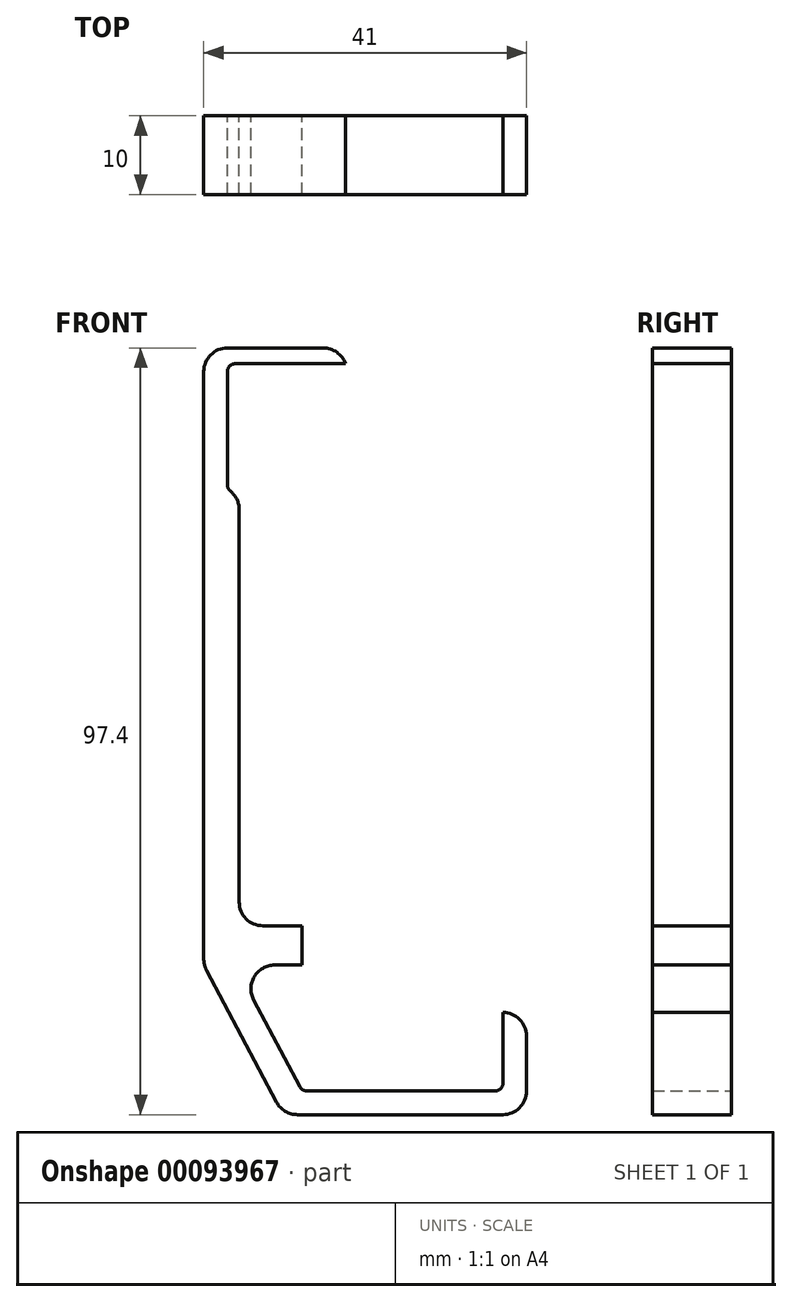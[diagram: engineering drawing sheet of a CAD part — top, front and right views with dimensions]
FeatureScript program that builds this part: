
annotation { "Feature Type Name" : "Feature", "Feature Type Description" : "" }
export const myFeature = defineFeature(function(context is Context, id is Id, definition is map)
    precondition{}
    {
        {
            var Q0;
            Q0=qCreatedBy(makeId("Front.planeOp"),FACE);
            var sketch = newSketch(context, id + "F0", { "sketchPlane" : qUnion([Q0])});
            skLineSegment(sketch, "E0.bottom", {"start": v(50, 8.2) * mm, "end": v(-50, 8.2) * mm});
            skLineSegment(sketch, "E0.top", {"start": v(50, -8.2) * mm, "end": v(-50, -8.2) * mm});
            skLineSegment(sketch, "E0.left", {"start": v(50, 8.2) * mm, "end": v(50, -8.2) * mm});
            skLineSegment(sketch, "E0.right", {"start": v(-50, 8.2) * mm, "end": v(-50, -8.2) * mm});
            skPoint(sketch, "E0.middle", {"position": v(0, 0) * mm});
            skLineSegment(sketch, "E1", {"start": v(-50, -8.2) * mm, "end": v(-40.5, -8.2) * mm});
            skLineSegment(sketch, "E2.bottom", {"start": v(-40.5, -8.2) * mm, "end": v(-15, -8.2) * mm});
            skLineSegment(sketch, "E2.top", {"start": v(-40.5, -84.2) * mm, "end": v(-15, -84.2) * mm});
            skLineSegment(sketch, "E2.left", {"start": v(-40.5, -8.2) * mm, "end": v(-40.5, -84.2) * mm});
            skLineSegment(sketch, "E2.right", {"start": v(-15, -8.2) * mm, "end": v(-15, -84.2) * mm});
            skLineSegment(sketch, "E3", {"start": v(-50, 8.2) * mm, "end": v(-35, 8.2) * mm});
            skLineSegment(sketch, "E4", {"start": v(-35, 8.2) * mm, "end": v(-35, 10.2) * mm});
            skLineSegment(sketch, "E5", {"start": v(-15, -84.2) * mm, "end": v(-15, -74.2) * mm});
            skLineSegment(sketch, "E6", {"start": v(-15, -74.2) * mm, "end": v(-12, -74.2) * mm});
            skLineSegment(sketch, "E7", {"start": v(-35, 10.2) * mm, "end": v(-53, 10.2) * mm});
            skLineSegment(sketch, "E8", {"start": v(-12, -74.2) * mm, "end": v(-12, -87.2) * mm});
            skLineSegment(sketch, "E9", {"start": v(-40.5, -8.2) * mm, "end": v(-40.5, -68.2) * mm});
            skLineSegment(sketch, "E10", {"start": v(-49, -68.2) * mm, "end": v(-40.5, -68.2) * mm});
            skLineSegment(sketch, "E11", {"start": v(-49, -68.2) * mm, "end": v(-40.5, -84.2) * mm});
            skPoint(sketch, "E12", {"position": v(-53, -68.2) * mm});
            skLineSegment(sketch, "E13", {"start": v(-53, 10.2) * mm, "end": v(-53, -68.2) * mm});
            skLineSegment(sketch, "E14", {"start": v(-40.5, -84.2) * mm, "end": v(-44.5, -84.2) * mm});
            skLineSegment(sketch, "E15", {"start": v(-49, -68.2) * mm, "end": v(-53, -68.2) * mm});
            skLineSegment(sketch, "E16", {"start": v(-44.5, -84.2) * mm, "end": v(-53, -68.2) * mm});
            skLineSegment(sketch, "E17", {"start": v(-44.5, -84.2) * mm, "end": v(-42.9, -87.2) * mm});
            skLineSegment(sketch, "E18", {"start": v(-42.9, -87.2) * mm, "end": v(-12, -87.2) * mm});
            skLineSegment(sketch, "E19", {"start": v(-40.5, -68.2) * mm, "end": v(-40.5, -63.2) * mm});
            skLineSegment(sketch, "E20", {"start": v(-40.5, -63.2) * mm, "end": v(-49, -63.2) * mm});
            skLineSegment(sketch, "E21", {"start": v(-49, -63.2) * mm, "end": v(-49, -68.2) * mm});
            skLineSegment(sketch, "E22", {"start": v(-48.5, -63.2) * mm, "end": v(-48.5, -8.2) * mm});
            skSolve(sketch);
        }
        {
            var Q0;
            Q0=makeQuery(id+"F0.imprint","IMPRINT",FACE,{"disambiguationData":[TD([[makeQuery(id+"F0.imprint","IMPRINT",EDGE,{"derivedFrom":sQuery(id+"F0.wireOp",EDGE,"E0.right")}),-1.0]])]});
            var Q1;
            Q1=makeQuery(id+"F0.imprint","IMPRINT",FACE,{"disambiguationData":[TD([[makeQuery(id+"F0.imprint","IMPRINT",EDGE,{"derivedFrom":sQuery(id+"F0.wireOp",EDGE,"E11")}),-1.0]])]});
            var Q2;
            Q2=makeQuery(id+"F0.imprint","IMPRINT",FACE,{"disambiguationData":[TD([[makeQuery(id+"F0.imprint","IMPRINT",EDGE,{"derivedFrom":sQuery(id+"F0.wireOp",EDGE,"E2.top")}),-1.0]])]});
            var Q3;
            Q3=makeQuery(id+"F0.imprint","IMPRINT",FACE,{"disambiguationData":[TD([[makeQuery(id+"F0.imprint","IMPRINT",EDGE,{"derivedFrom":sQuery(id+"F0.wireOp",EDGE,"lY91cw5x-jmdy-KzeB-PsSb-3NSYwBVOxv6V.bottom")}),-1.0]])]});
            var Q4;
            Q4=makeQuery(id+"F0.imprint","IMPRINT",FACE,{"disambiguationData":[TD([[makeQuery(id+"F0.imprint","IMPRINT",EDGE,{"derivedFrom":sQuery(id+"F0.wireOp",EDGE,"uIQLEJby-xmbG-Ts80-sez8-3mGEYaDvUWFH")}),1.0]])]});
            var Q5;
            Q5=makeQuery(id+"F0.imprint","IMPRINT",FACE,{"disambiguationData":[TD([[makeQuery(id+"F0.imprint","IMPRINT",EDGE,{"derivedFrom":sQuery(id+"F0.wireOp",EDGE,"E10")}),1.0]])]});
            extrude(context, id + "F1", {"entities" : qUnion([Q0, Q1, Q2, Q3, Q4, Q5]), "depth" : 10 * mm});
        }
        {
            var Q0;
            Q0=makeQuery(id+"F1.opExtrude","SWEPT_EDGE",EDGE,{"disambiguationData":[OSD([sQuery(id+"F0.wireOp",EDGE,"E7"),sQuery(id+"F0.wireOp",EDGE,"E13")])]});
            var Q1;
            Q1=makeQuery(id+"F1.opExtrude","SWEPT_EDGE",EDGE,{"disambiguationData":[OSD([sQuery(id+"F0.wireOp",EDGE,"E4"),sQuery(id+"F0.wireOp",EDGE,"E7")])]});
            var Q2;
            Q2=makeQuery(id+"F1.opExtrude","SWEPT_EDGE",EDGE,{"disambiguationData":[OSD([sQuery(id+"F0.wireOp",EDGE,"E6"),sQuery(id+"F0.wireOp",EDGE,"E8")])]});
            var Q3;
            Q3=makeQuery(id+"F1.opExtrude","SWEPT_EDGE",EDGE,{"disambiguationData":[OSD([sQuery(id+"F0.wireOp",EDGE,"E8"),sQuery(id+"F0.wireOp",EDGE,"E18")])]});
            var Q4;
            Q4=makeQuery(id+"F1.opExtrude","SWEPT_EDGE",EDGE,{"disambiguationData":[OSD([sQuery(id+"F0.wireOp",EDGE,"E17"),sQuery(id+"F0.wireOp",EDGE,"E18")])]});
            var Q5;
            Q5=makeQuery(id+"F1.opExtrude","SWEPT_EDGE",EDGE,{"disambiguationData":[OSD([sQuery(id+"F0.wireOp",EDGE,"E13"),sQuery(id+"F0.wireOp",EDGE,"E15"),sQuery(id+"F0.wireOp",EDGE,"E16")])]});
            fillet(context, id + "F2", {"entities" : qUnion([Q0, Q1, Q2, Q3, Q4, Q5]), "radius" : 3 * mm, "tangentPropagation" : true, "allowEdgeOverflow" : false});
        }
        {
            var Q0;
            Q0=makeQuery(id+"F1.opExtrude","SWEPT_EDGE",EDGE,{"disambiguationData":[OSD([sQuery(id+"F0.wireOp",EDGE,"E2.top"),sQuery(id+"F0.wireOp",EDGE,"E2.left"),sQuery(id+"F0.wireOp",EDGE,"E11"),sQuery(id+"F0.wireOp",EDGE,"E14")])]});
            var Q1;
            Q1=makeQuery(id+"F1.opExtrude","SWEPT_EDGE",EDGE,{"disambiguationData":[OSD([sQuery(id+"F0.wireOp",EDGE,"E2.top"),sQuery(id+"F0.wireOp",EDGE,"E5")])]});
            var Q2;
            Q2=makeQuery(id+"F1.opExtrude","SWEPT_EDGE",EDGE,{"disambiguationData":[OSD([sQuery(id+"F0.wireOp",EDGE,"E0.right"),sQuery(id+"F0.wireOp",EDGE,"E3")])]});
            fillet(context, id + "F3", {"entities" : qUnion([Q0, Q1, Q2]), "radius" : 1 * mm, "tangentPropagation" : true, "allowEdgeOverflow" : false});
        }
        {
            var Q0;
            Q0=makeQuery(id+"F1.opExtrude","SWEPT_EDGE",EDGE,{"disambiguationData":[OSD([sQuery(id+"F0.wireOp",EDGE,"E10"),sQuery(id+"F0.wireOp",EDGE,"E11"),sQuery(id+"F0.wireOp",EDGE,"E15"),sQuery(id+"F0.wireOp",EDGE,"E21")])]});
            var Q1;
            Q1=makeQuery(id+"F1.opExtrude","SWEPT_EDGE",EDGE,{"disambiguationData":[OSD([sQuery(id+"F0.wireOp",EDGE,"E1"),sQuery(id+"F0.wireOp",EDGE,"E22")])]});
            var Q2;
            Q2=makeQuery(id+"F1.opExtrude","SWEPT_EDGE",EDGE,{"disambiguationData":[OSD([sQuery(id+"F0.wireOp",EDGE,"E20"),sQuery(id+"F0.wireOp",EDGE,"E22")])]});
            fillet(context, id + "F4", {"entities" : qUnion([Q0, Q1, Q2]), "radius" : 3 * mm, "tangentPropagation" : true, "allowEdgeOverflow" : false});
        }
    });
